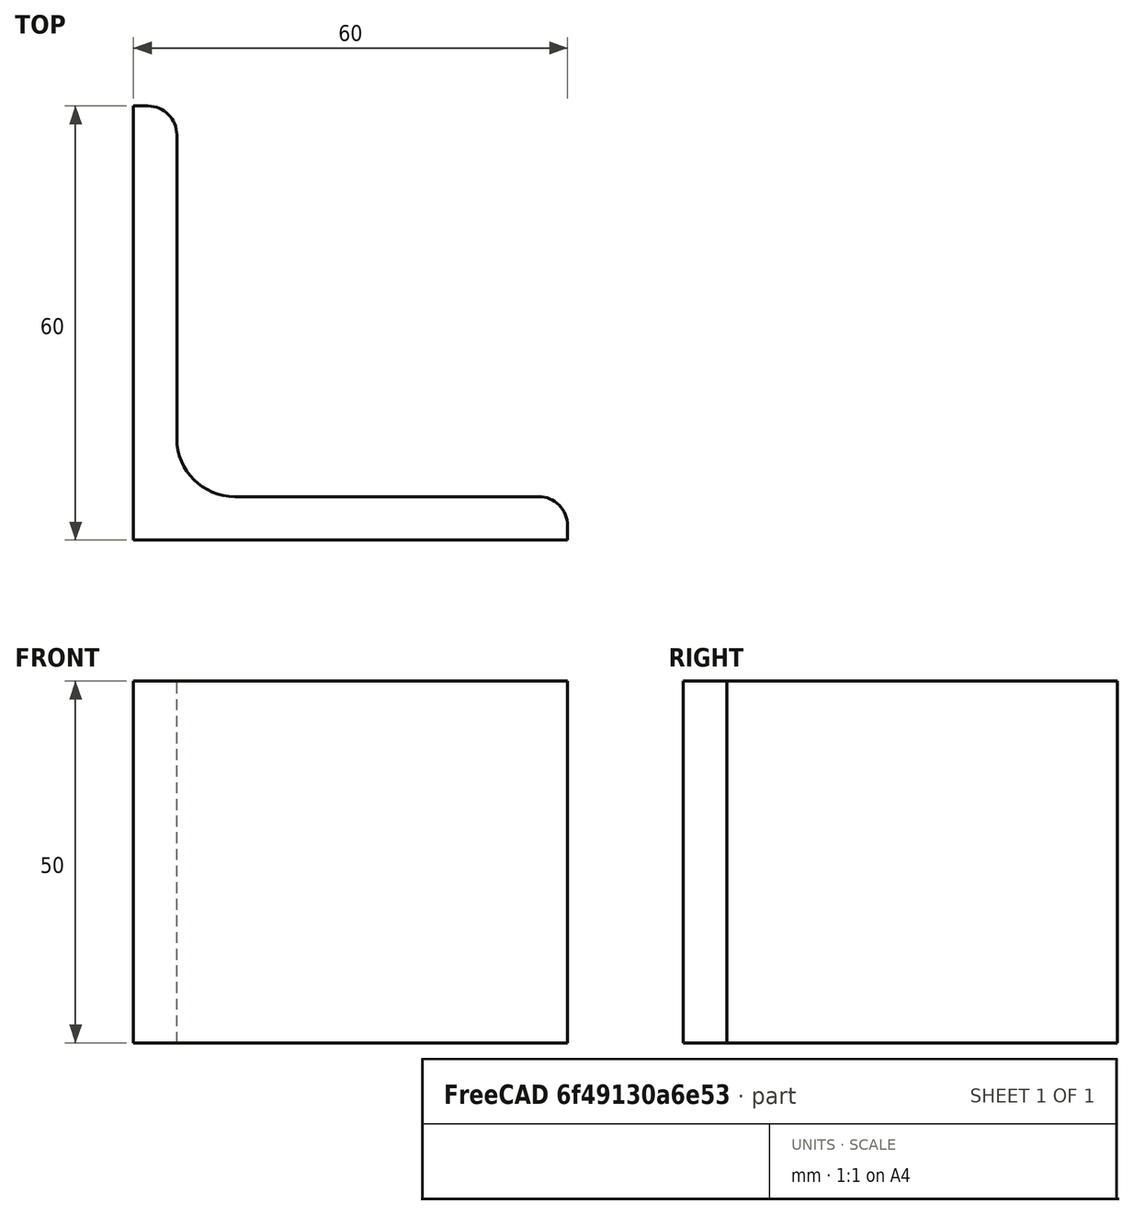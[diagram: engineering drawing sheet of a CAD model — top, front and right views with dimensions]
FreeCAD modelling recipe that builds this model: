
FCSTD DOCUMENT  (FreeCAD 0.15R4671 (Git))
Label: Angle Bar L60x60x6 EN10056 S235JR
License: All rights reserved
LicenseURL: http://en.wikipedia.org/wiki/All_rights_reserved
objects: Sketcher::SketchObject×1, Part::Extrusion×1
note: 2 computed .brp shape members not serialized (recipe doc carries the construction recipe); baked Part::Feature solids carry a one-line shape summary decoded from their .brp

FEATURE [Sketcher::SketchObject] Sketch
  sketch-geometry (9):
    g0: LineSegment StartX=0 StartY=0 StartZ=0 EndX=60 EndY=0 EndZ=0
    g1: LineSegment StartX=60 StartY=0 StartZ=0 EndX=60 EndY=2 EndZ=0
    g2: LineSegment StartX=56 StartY=6 StartZ=0 EndX=14 EndY=6 EndZ=0
    g3: LineSegment StartX=0 StartY=0 StartZ=0 EndX=0 EndY=60 EndZ=0
    g4: LineSegment StartX=0 StartY=60 StartZ=0 EndX=2 EndY=60 EndZ=0
    g5: LineSegment StartX=6 StartY=56 StartZ=0 EndX=6 EndY=14 EndZ=0
    g6: ArcOfCircle CenterX=14 CenterY=14 CenterZ=0 NormalX=0 NormalY=0 NormalZ=1 Radius=8 StartAngle=3.14159 EndAngle=4.71239
    g7: ArcOfCircle CenterX=2 CenterY=56 CenterZ=0 NormalX=0 NormalY=0 NormalZ=1 Radius=4 StartAngle=0 EndAngle=1.5708
    g8: ArcOfCircle CenterX=56 CenterY=2 CenterZ=0 NormalX=0 NormalY=0 NormalZ=1 Radius=4 StartAngle=0 EndAngle=1.5708
  constraints (23):
    c: Coincident(g0,g-1)
    c: Horizontal(g0)
    c: Coincident(g1,g0)
    c: Vertical(g1)
    c: Horizontal(g2)
    c: Coincident(g3,g-1)
    c: Vertical(g3)
    c: Coincident(g4,g3)
    c: Horizontal(g4)
    c: Vertical(g5)
    c: Tangent(g5,g6) = -1.5708
    c: Tangent(g2,g6) = 1.5708
    c: Tangent(g4,g7) = 1.5708
    c: Tangent(g5,g7) = 1.5708
    c: Tangent(g2,g8) = -1.5708
    c: Tangent(g1,g8) = -1.5708
    c: DistanceX(g0) = 60
    c: DistanceY(g3) = 60
    c: DistanceY(g0,g2) = 6
    c: DistanceX(g3,g5) = 6
    c: Radius(g6) = 8
    c: Radius(g8) = 4
    c: Radius(g7) = 4
FEATURE [Part::Extrusion] Extrude  label="Angle Bar L60x60x6 EN10056 S235JR"
  Base = -> Sketch
  Dir = (0,0,50)
  Solid = true
